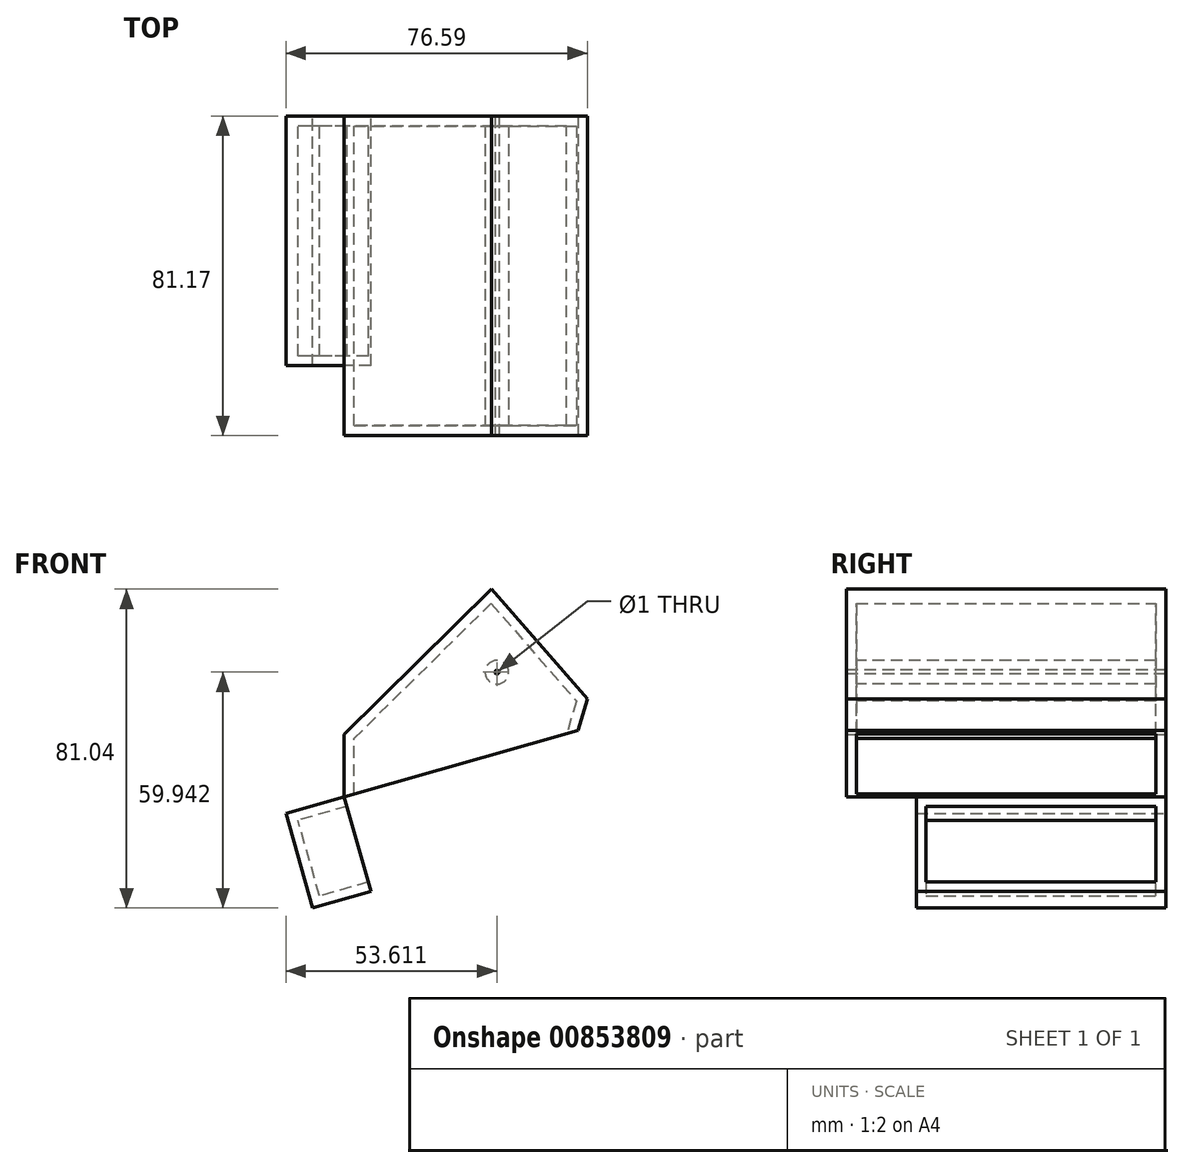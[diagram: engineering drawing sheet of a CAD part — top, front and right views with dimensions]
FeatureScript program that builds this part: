
annotation { "Feature Type Name" : "Feature", "Feature Type Description" : "" }
export const myFeature = defineFeature(function(context is Context, id is Id, definition is map)
    precondition{}
    {
        {
            var Q0;
            Q0=qCreatedBy(makeId("Front.planeOp"),FACE);
            var sketch = newSketch(context, id + "F0", { "sketchPlane" : qUnion([Q0])});
            skLineSegment(sketch, "E0", {"start": v(-39.4, -38.18) * mm, "end": v(44.1, 44.1) * mm});
            skLineSegment(sketch, "E1", {"start": v(44.1, 44.1) * mm, "end": v(-34.3, 44.1) * mm});
            skLineSegment(sketch, "E2", {"start": v(-34.3, 44.1) * mm, "end": v(31.45, -31.24) * mm});
            skLineSegment(sketch, "E3", {"start": v(31.45, -31.24) * mm, "end": v(-35.53, -50.23) * mm});
            skLineSegment(sketch, "E4", {"start": v(-35.53, -50.23) * mm, "end": v(-35.53, -34.36) * mm});
            skSolve(sketch);
        }
        {
            var Q0;
            {var subQ4=sQuery(id+"F0.wireOp",EDGE,"E3");Q0=makeQuery(id+"F0.imprint","IMPRINT",FACE,{"disambiguationData":[TD([[makeQuery(id+"F0.imprint","IMPRINT",EDGE,{"derivedFrom":subQ4}),-1.0]])]});}
            extrude(context, id + "F1", {"entities" : qUnion([Q0]), "depth" : 81.17 * mm, "offsetDistance" : 25 * mm});
        }
        {
            var Q0;
            Q0=makeQuery(id+"F1.opExtrude","SWEPT_EDGE",EDGE,{"disambiguationData":[OSD([sQuery(id+"F0.wireOp",EDGE,"E2"),sQuery(id+"F0.wireOp",EDGE,"E3")])]});
            chamfer(context, id + "F2", {"entities" : qUnion([Q0]), "width" : 5 * mm, "tangentPropagation" : true});
        }
        {
            var Q0;
            Q0=makeQuery(id+"F1.opExtrude","CAP_FACE",FACE,{"disambiguationData":[OSD([sQuery(id+"F0.wireOp",EDGE,"E0"),sQuery(id+"F0.wireOp",EDGE,"E2"),sQuery(id+"F0.wireOp",EDGE,"E3"),sQuery(id+"F0.wireOp",EDGE,"E4")])],"isStart":false});
            var sketch = newSketch(context, id + "F3", { "sketchPlane" : qUnion([Q0])});
            skCircle(sketch, "E5", {"center": v(0, -23.2) * mm, "radius": 11.3 * mm});
            skSolve(sketch);
        }
        {
            var Q0;
            Q0=makeQuery(id+"F3.imprint","IMPRINT",FACE,{"disambiguationData":[TD([[makeQuery(id+"F3.imprint","IMPRINT",EDGE,{"derivedFrom":sQuery(id+"F3.wireOp",EDGE,"E5")}),1.0]])]});
            var sketch = newSketch(context, id + "F4", { "sketchPlane" : qUnion([Q0])});
            skCircle(sketch, "E6", {"center": v(3.28, -18.54) * mm, "radius": 3.1 * mm});
            skSolve(sketch);
        }
        {
            var Q0;
            Q0=sQuery(id+"F4.wireOp",VERTEX,"E6.center");
            var Q1;
            Q1=makeQuery(id+"F1.opExtrude","SWEPT_BODY",BODY,{"disambiguationData":[OSD([sQuery(id+"F0.wireOp",EDGE,"E0"),sQuery(id+"F0.wireOp",EDGE,"E2"),sQuery(id+"F0.wireOp",EDGE,"E3"),sQuery(id+"F0.wireOp",EDGE,"E4")])]});
            hole(context, id + "F5", {"style" : HoleStyle.SIMPLE, "endStyle" : HoleEndStyle.THROUGH, "holeDiameter" : 1 * mm, "majorDiameter" : 5 * mm, "isTappedThrough" : true, "tappedDepth" : 12 * mm, "tapClearance" : 3, "locations" : qUnion([Q0]), "scope" : qUnion([Q1])});
        }
        {
            var Q0;
            Q0=makeQuery(id+"F1.opExtrude","SWEPT_FACE",FACE,{"disambiguationData":[OSD([sQuery(id+"F0.wireOp",EDGE,"E3")])]});
            var sketch = newSketch(context, id + "F6", { "sketchPlane" : qUnion([Q0])});
            skLineSegment(sketch, "E7.bottom", {"start": v(-31.33, 63.42) * mm, "end": v(-63.27, 63.42) * mm});
            skLineSegment(sketch, "E7.top", {"start": v(-31.33, 0) * mm, "end": v(-63.27, 0) * mm});
            skLineSegment(sketch, "E7.left", {"start": v(-31.33, 63.42) * mm, "end": v(-31.33, 0) * mm});
            skLineSegment(sketch, "E7.right", {"start": v(-63.27, 63.42) * mm, "end": v(-63.27, 0) * mm});
            skSolve(sketch);
        }
        {
            var Q0;
            {var subQ0=sQuery(id+"F6.wireOp",EDGE,"E7.right");Q0=makeQuery(id+"F6.imprint","IMPRINT",FACE,{"disambiguationData":[TD([[makeQuery(id+"F6.imprint","IMPRINT",EDGE,{"derivedFrom":subQ0}),1.0]])]});}
            extrude(context, id + "F7", {"entities" : qUnion([Q0]), "depth" : 25 * mm, "offsetDistance" : 25 * mm});
        }
        {
            var Q0;
            Q0=makeQuery(id+"F7.opExtrude","SWEPT_FACE",FACE,{"disambiguationData":[OSD([sQuery(id+"F0.wireOp",EDGE,"E3"),sQuery(id+"F0.wireOp",EDGE,"E4")])]});
            var Q1;
            Q1=makeQuery(id+"F1.opExtrude","SWEPT_FACE",FACE,{"disambiguationData":[OSD([sQuery(id+"F0.wireOp",EDGE,"E3")])]});
            shell(context, id + "F8", {"entities" : qUnion([Q0, Q1]), "thickness" : 2.5 * mm});
        }
    });
